# Revit family: Diffuser-Carnes-DASD-w-Center _T-1_Slot
name_source: partatom
category: Duct Accessories
revit_build: Autodesk Revit Architecture 2012 (Build: 20110309_2315(x64)
units: mm (PartAtom-declared; Revit-internal decimal feet)

## types (24) — shared parameters
Catalog = http://www.carnes.com
Default Elevation = 0"
Description = Plenum Slot Diffusers
Duct Height = 4"
Duct Width = 6"
Half Inlet Width = 3"
Inlet Nominal Size Height D = 3 1/2"
Inlet Nominal Size Width = 6"
Manufacturer = CARNES COMPANY
Model = DASD
Product Page URL = http://www.carnes.com
Specification Sheet = http://www.carnes.com
Subcatagory = Air Distribution
Supply Connection = Diffuser Supply Connector
Supply Connector = Yes
URL = http://www.carnes.com
Unit = Metal - Carnes - Steel Galvanized

## per-type parameters (varying)
| type | Depth | Height C | Length | Slot Opening A |
| DASD 24 x 8 x3/4 | 3 1/2" | 8" | 24" | 3/4" |
| DASD 24 x 11 x3/4 | 3 1/2" | 11" | 24" | 3/4" |
| DASD 24 x 8 x1 | 4" | 8" | 24" | 1" |
| DASD 24 x 11 x1 | 4" | 11" | 24" | 1" |
| DASD 24 x 8 x1.5 | 5" | 8" | 24" | 1 1/2" |
| DASD 24 x 11 x1.5 | 5" | 11" | 24" | 1 1/2" |
| DASD 30 x 8 x3/4 | 3 1/2" | 8" | 30" | 3/4" |
| DASD 30 x 11 x3/4 | 3 1/2" | 11" | 30" | 3/4" |
| DASD 30 x 8 x1 | 4" | 8" | 30" | 1" |
| DASD 30 x 11 x1 | 4" | 11" | 30" | 1" |
| DASD 30 x 8 x1.5 | 5" | 8" | 30" | 1 1/2" |
| DASD 30 x 11 x1.5 | 5" | 11" | 30" | 1 1/2" |
| DASD 48 x 8 x3/4 | 3 1/2" | 8" | 48" | 3/4" |
| DASD 48 x 11 x3/4 | 3 1/2" | 11" | 48" | 3/4" |
| DASD 48 x 8 x1 | 4" | 8" | 48" | 1" |
| DASD 48 x 11 x1 | 4" | 11" | 48" | 1" |
| DASD 48 x 8 x1.5 | 5" | 8" | 48" | 1 1/2" |
| DASD 48 x 11 x1.5 | 5" | 11" | 48" | 1 1/2" |
| DASD 60 x 8 x3/4 | 3 1/2" | 8" | 60" | 3/4" |
| DASD 60 x 11 x3/4 | 3 1/2" | 11" | 60" | 3/4" |
| DASD 60 x 8 x1 | 4" | 8" | 60" | 1" |
| DASD 60 x 11 x1 | 4" | 11" | 60" | 1" |
| DASD 60 x 8 x1.5 | 5" | 8" | 60" | 1 1/2" |
| DASD 60 x 11 x1.5 | 5" | 11" | 60" | 1 1/2" |

## geometry (parser evidence)
native form markers: Blend x2, Sweep x3
no freeform markers — native parametric forms only
